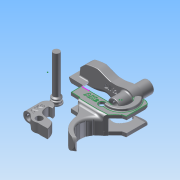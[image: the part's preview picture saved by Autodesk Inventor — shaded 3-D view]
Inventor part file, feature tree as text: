
AUTODESK INVENTOR PART (.ipt)
format: ipt  version: 2012 (Build 160160000, 160)  size: 2,872,320 bytes
history: native  units: mm
features: fillet x13, chamfer x7, sketch x6, imported_body x4, emboss x3, extrude x2, other x1
ambient origin geometry x8: Origin, YZ Plane, XZ Plane, XY Plane, X Axis, Y Axis, Z Axis, Center Point
bodies: Solid1 (feature_tree), Solid5 (feature_tree), Solid6 (feature_tree)
feature tree (36):
  other  "trace_v8_export.igs1"
  fillet  "Fillet1"  Radius=0.9mm
  chamfer  "Chamfer1"  Distance=0.5mm Angle=45.0deg
  fillet  "Fillet5"  Radius=3.5mm
  fillet  "Fillet6"  [1 undecoded]
  fillet  "Fillet7"  [1 undecoded]
  fillet  "Fillet8"  Radius=3.5mm
  fillet  "Fillet9"  Radius=0.5mm
  chamfer  "Chamfer2"  Distance=0.5mm Angle=45.0deg
  chamfer  "Chamfer3"  Distance=0.5mm Angle=45.0deg
  chamfer  "Chamfer4"  Distance=0.5mm Angle=45.0deg
  fillet  "Fillet10"  Radius=2.0mm
  sketch  "Sketch2"  dims[d12=1.5mm d13=0.0mm d14=1.5mm d15=5.51903mm d16=0.5mm d17=7.44247mm d18=0.0mm d19=1.5mm d20=0.5mm d21=2.55mm d22=1.5mm d23=4.032mm]
  sketch  "Sketch3"  dims[d24=3.0mm]
  sketch  "Sketch4"  dims[d25=0.5mm]
  emboss  "Emboss1"
  emboss  "Emboss2"
  emboss  "Emboss3"
  fillet  "Fillet16"  Radius=0.4mm
  extrude  "Extrusion1"  Depth=0.7mm TaperAngle=0.0deg
  fillet  "Fillet17"  Radius=0.5mm
  sketch  "Sketch6"  dims[d39=0.5mm d40=0.0mm d41=0.7mm d42=0.0mm d86=0.5mm d87=2.0mm d88=0.0mm]
  fillet  "Fillet18"  Radius=2.0mm
  chamfer  "Chamfer5"  [1 undecoded]
  chamfer  "Chamfer6"  Distance=0.2mm Angle=45.0deg
  chamfer  "Chamfer7"  Distance=0.2mm Angle=45.0deg
  extrude  "Extrusion2"  Depth=0.2mm TaperAngle=45.0deg
  fillet  "Fillet19"  Radius=15.0mm
  fillet  "Fillet20"  [1 undecoded]
  fillet  "Fillet21"  Radius=0.5mm
  imported_body  "Base1"
  imported_body  "Base5"
  imported_body  "Base6"
  imported_body  "Base7"
  sketch  "Sketch5"  dims[d26=0.42mm d27=0.5mm d28=2.0mm d29=45.0deg d30=0.5mm d31=2.0mm d32=45.0deg d33=0.5mm d34=2.0mm d35=45.0deg d36=2.0mm d37=0.4mm d38=0.0mm]
  sketch  "Sketch7"  dims[d89=0.6mm d90=0.0mm d91=1.6mm d92=0.8mm d93=3.632mm d94=0.0mm d95=1.60386mm d96=0.0mm d97=1.32298mm d98=0.6mm d99=9.2528mm d100=0.6mm d101=4.43325mm d102=0.6mm d103=0.35654mm d104=0.2mm d105=2.0mm d106=45.0deg d107=0.2mm d108=2.0mm d109=45.0deg d110=0.2mm d111=2.0mm d112=45.0deg d117=15.0mm d118=0.0mm d120=0.0mm d121=1.0mm d122=9.11366mm d123=1.0mm d124=1.59169mm d125=0.0mm d126=0.2mm d127=0.0mm d128=0.0mm d129=0.0mm d130=0.2mm d131=1.0mm d132=1.456mm d133=1.0mm d134=9.46277mm d135=0.0mm d136=0.5mm]
note: 4 required parameter values undecoded (feature->parameter linkage not recoverable at this tier; creation-order binding heuristic only, values carry confidence <= 0.55)
